# Revit family: steigeleiter_6_FT_FTSO_FTK_A2_A4.600rfa
name_source: partatom
category: Generic Models
revit_build: Autodesk Revit 2017 (Build: 20160225_1515(x64)
units: mm (PartAtom-declared; Revit-internal decimal feet)

## family parameters
Always vertical = Yes
Can host rebar = No
Cut with Voids When Loaded = No
Part Type = Normal
Room Calculation Point = No
Round Connector Dimension = Use Diameter
Shared = No
Work Plane-Based = No

## types (3) — shared parameters
Cut's number = 60
Cut's number 2 = 5
Cut's number 3 = 2
Cut's space = 50 mm  [stored 0.164042 ft]
Cut's space 2 = 600 mm  [stored 1.9685 ft]
Length = 3000 mm  [stored 9.84252 ft]
Length 2 = 274 mm
Manufacturer = OBO BETTERMANN
URL = http://www.obo-bettermann.com
Width = 600 mm  [stored 1.9685 ft]
Width 1 = 300 mm

## per-type parameters (varying)
| type | GTIN | Manufacturer Art.No. | Material |
| SLM 50 C40 6 FT | 4012196168859 | 6010504 | Polyester |
| SLM50C406FTKAGR | 4012196681648 | 6010580 | Polyester |
| SLM50C40 6FTK RW | 4012196691357 | 6010581 | Polyester / Epoxid |

note: column(s) folded — value = type name in every type: Article Type

note: [stored X ft] marks values corroborated as IEEE doubles in the binary element streams (Revit-internal decimal feet)

## geometry (parser evidence)
native form markers: Sweep x1
no freeform markers — native parametric forms only
